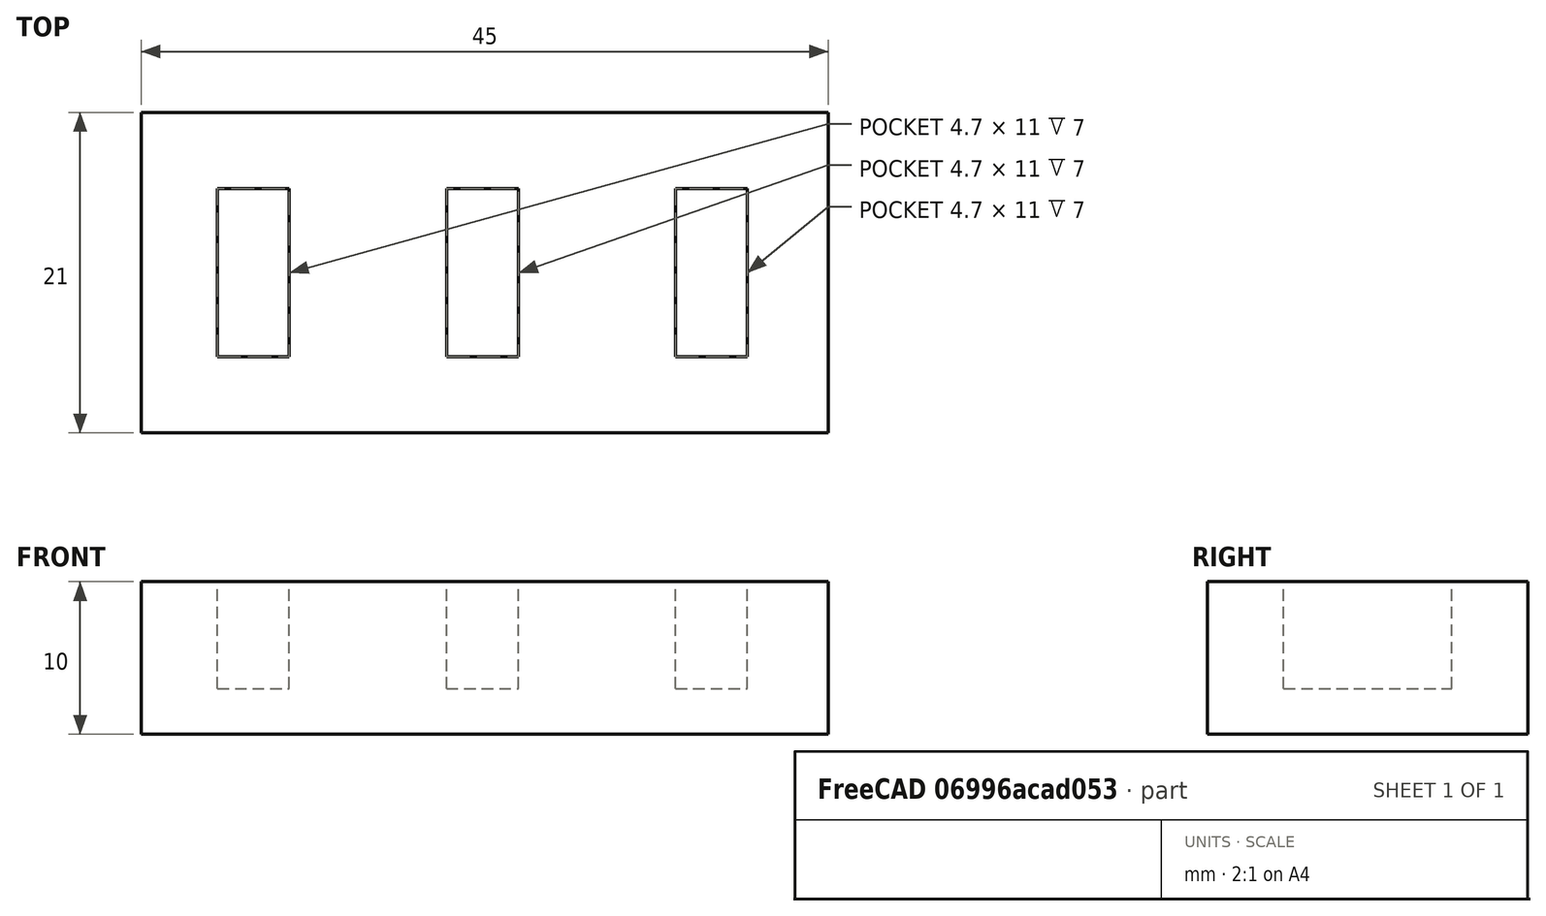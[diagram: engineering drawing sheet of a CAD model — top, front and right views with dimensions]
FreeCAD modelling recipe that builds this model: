
FCSTD DOCUMENT  (FreeCAD 0.21R33694 (Git))
Label: OJT1_T08P01_portapendrives
License: All rights reserved
LicenseURL: http://en.wikipedia.org/wiki/All_rights_reserved
objects: Part::Box×4, Part::MultiFuse×1, Part::Cut×1
note: 6 computed .brp shape members not serialized (recipe doc carries the construction recipe); baked Part::Feature solids carry a one-line shape summary decoded from their .brp

FEATURE [Part::Box] Box  label="Ranura 1"
  AttacherType = Attacher::AttachEngine3D
  Height = 12
  Length = 4.7
  Width = 11
FEATURE [Part::Box] Box001  label="Ranura 2"
  AttacherType = Attacher::AttachEngine3D
  Height = 12
  Length = 4.7
  Placement = pos=(15,0,0) rot=(0,0,1;0rad)
  Width = 11
FEATURE [Part::Box] Box002  label="Ranura 3"
  AttacherType = Attacher::AttachEngine3D
  Height = 12
  Length = 4.7
  Placement = pos=(30,0,0) rot=(0,0,1;0rad)
  Width = 11
FEATURE [Part::MultiFuse] Fusion  label="Ranuras"
  Placement = pos=(5,5,3) rot=(0,0,1;0rad)
  Refine = true
  Shapes = -> [Box002,Box001,Box]
FEATURE [Part::Box] Box003  label="Base"
  AttacherType = Attacher::AttachEngine3D
  Height = 10
  Length = 45
  Width = 21
FEATURE [Part::Cut] Cut  label="Porta_pendrives"
  Base = -> Box003
  Refine = true
  Tool = -> Fusion
